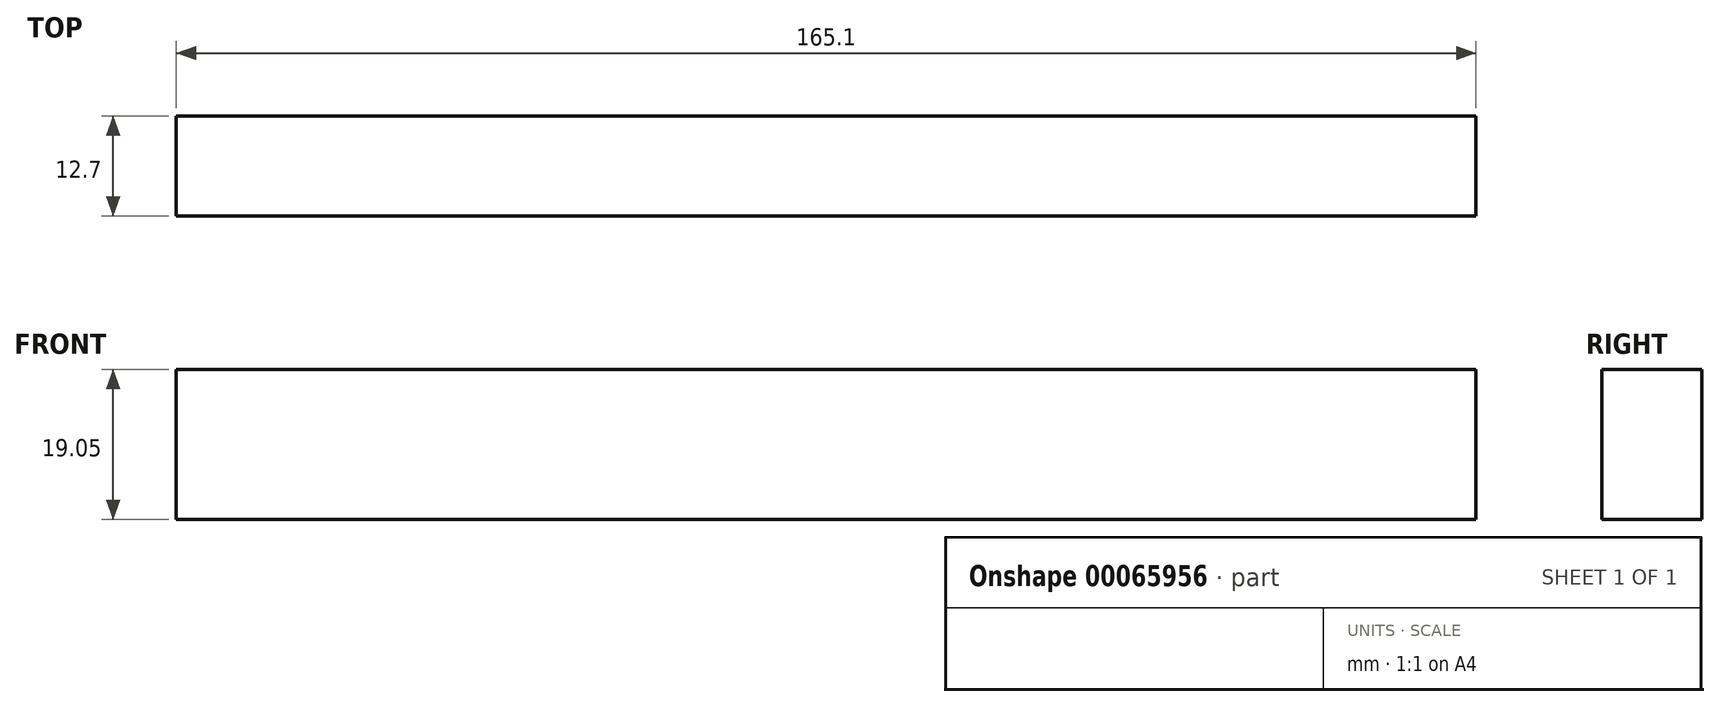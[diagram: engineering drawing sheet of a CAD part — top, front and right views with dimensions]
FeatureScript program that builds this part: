
annotation { "Feature Type Name" : "Feature", "Feature Type Description" : "" }
export const myFeature = defineFeature(function(context is Context, id is Id, definition is map)
    precondition{}
    {
        {
            var Q0;
            Q0=qCreatedBy(makeId("Front.planeOp"),FACE);
            var sketch = newSketch(context, id + "F0", { "sketchPlane" : qUnion([Q0])});
            skLineSegment(sketch, "E0.bottom", {"start": v(-66.84, 0) * mm, "end": v(98.26, 0) * mm});
            skLineSegment(sketch, "E0.top", {"start": v(-66.84, -19.05) * mm, "end": v(98.26, -19.05) * mm});
            skLineSegment(sketch, "E0.left", {"start": v(-66.84, 0) * mm, "end": v(-66.84, -19.05) * mm});
            skLineSegment(sketch, "E0.right", {"start": v(98.26, 0) * mm, "end": v(98.26, -19.05) * mm});
            skSolve(sketch);
        }
        {
            var Q0;
            Q0=makeQuery(id+"F0.imprint","IMPRINT",FACE,{"disambiguationData":[TD([[makeQuery(id+"F0.imprint","IMPRINT",EDGE,{"derivedFrom":sQuery(id+"F0.wireOp",EDGE,"E0.bottom")}),-1.0]])]});
            extrude(context, id + "F1", {"entities" : qUnion([Q0]), "depth" : 12.7 * mm});
        }
    });
